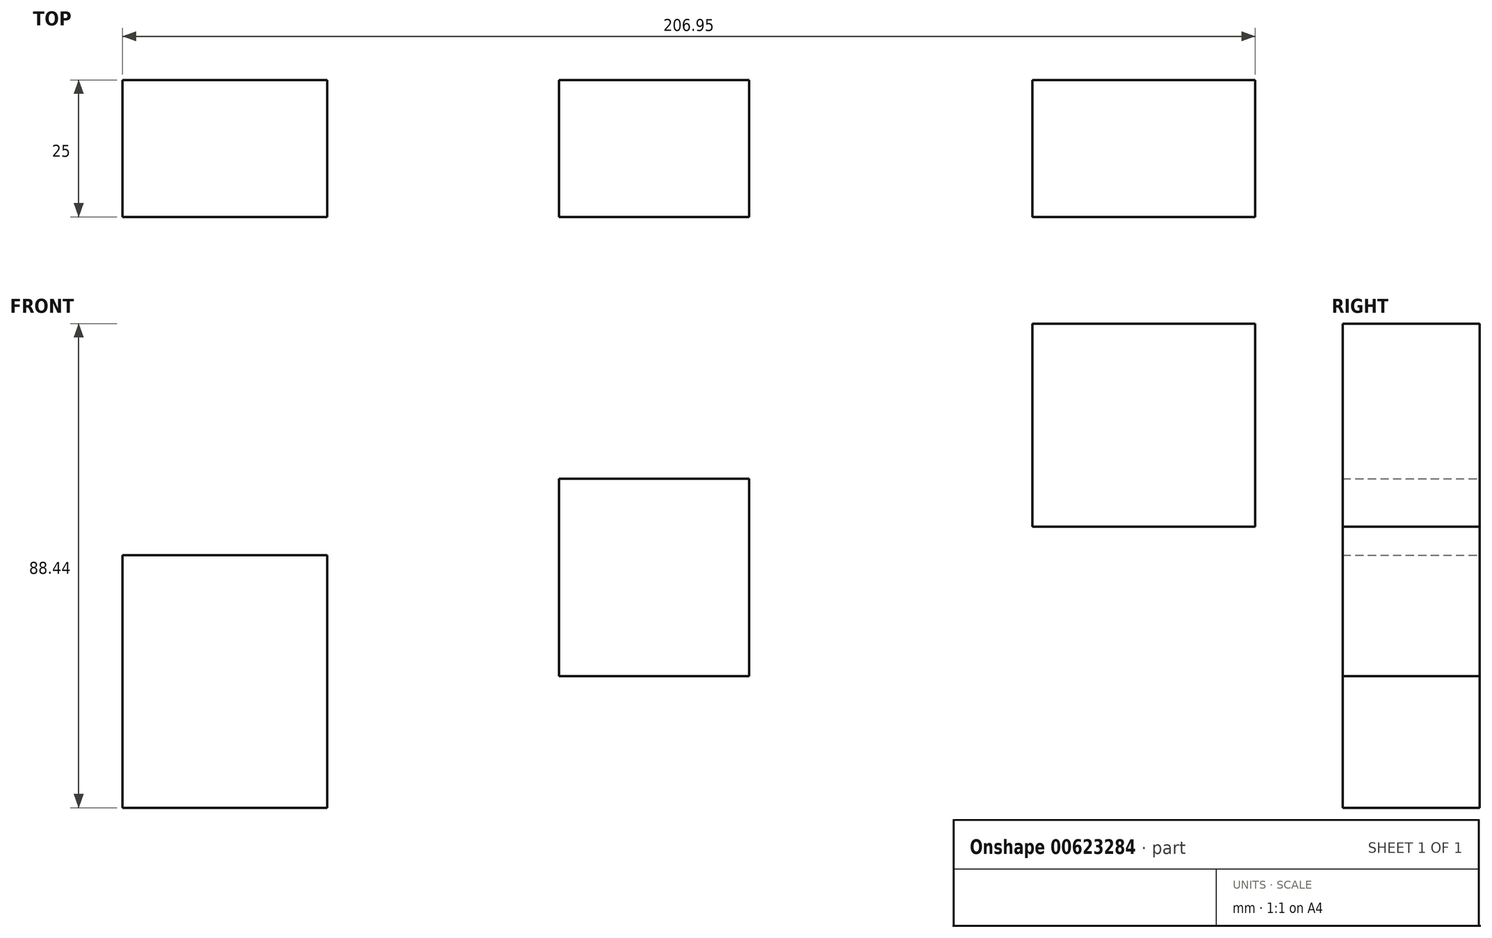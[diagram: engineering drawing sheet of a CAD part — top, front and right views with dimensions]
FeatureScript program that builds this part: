
annotation { "Feature Type Name" : "Feature", "Feature Type Description" : "" }
export const myFeature = defineFeature(function(context is Context, id is Id, definition is map)
    precondition{}
    {
        {
            var Q0;
            Q0=qCreatedBy(makeId("Front.planeOp"),FACE);
            var sketch = newSketch(context, id + "F0", { "sketchPlane" : qUnion([Q0])});
            skLineSegment(sketch, "E0.bottom", {"start": v(-144.03, -7.36) * mm, "end": v(-106.64, -7.36) * mm});
            skLineSegment(sketch, "E0.top", {"start": v(-144.03, 38.8) * mm, "end": v(-106.64, 38.8) * mm});
            skLineSegment(sketch, "E0.left", {"start": v(-144.03, -7.36) * mm, "end": v(-144.03, 38.8) * mm});
            skLineSegment(sketch, "E0.right", {"start": v(-106.64, -7.36) * mm, "end": v(-106.64, 38.8) * mm});
            skPoint(sketch, "E0.middle", {"position": v(-125.34, 15.72) * mm});
            skLineSegment(sketch, "E1.bottom", {"start": v(-64.25, 16.67) * mm, "end": v(-29.54, 16.67) * mm});
            skLineSegment(sketch, "E1.top", {"start": v(-64.25, 52.72) * mm, "end": v(-29.54, 52.72) * mm});
            skLineSegment(sketch, "E1.left", {"start": v(-64.25, 16.67) * mm, "end": v(-64.25, 52.72) * mm});
            skLineSegment(sketch, "E1.right", {"start": v(-29.54, 16.67) * mm, "end": v(-29.54, 52.72) * mm});
            skPoint(sketch, "E1.middle", {"position": v(-46.9, 34.7) * mm});
            skLineSegment(sketch, "E2.bottom", {"start": v(22.2, 43.96) * mm, "end": v(62.92, 43.96) * mm});
            skLineSegment(sketch, "E2.top", {"start": v(22.2, 81.08) * mm, "end": v(62.92, 81.08) * mm});
            skLineSegment(sketch, "E2.left", {"start": v(22.2, 43.96) * mm, "end": v(22.2, 81.08) * mm});
            skLineSegment(sketch, "E2.right", {"start": v(62.92, 43.96) * mm, "end": v(62.92, 81.08) * mm});
            skPoint(sketch, "E2.middle", {"position": v(42.56, 62.52) * mm});
            skSolve(sketch);
        }
        {
            var Q0;
            Q0=makeQuery(id+"F0.imprint","IMPRINT",FACE,{"disambiguationData":[TD([[makeQuery(id+"F0.imprint","IMPRINT",EDGE,{"derivedFrom":sQuery(id+"F0.wireOp",EDGE,"E0.bottom")}),1.0]])]});
            var Q1;
            Q1=makeQuery(id+"F0.imprint","IMPRINT",FACE,{"disambiguationData":[TD([[makeQuery(id+"F0.imprint","IMPRINT",EDGE,{"derivedFrom":sQuery(id+"F0.wireOp",EDGE,"E1.bottom")}),1.0]])]});
            var Q2;
            Q2=makeQuery(id+"F0.imprint","IMPRINT",FACE,{"disambiguationData":[TD([[makeQuery(id+"F0.imprint","IMPRINT",EDGE,{"derivedFrom":sQuery(id+"F0.wireOp",EDGE,"E2.bottom")}),1.0]])]});
            extrude(context, id + "F1", {"entities" : qUnion([Q0, Q1, Q2]), "depth" : 25 * mm, "offsetDistance" : 25 * mm});
        }
    });
